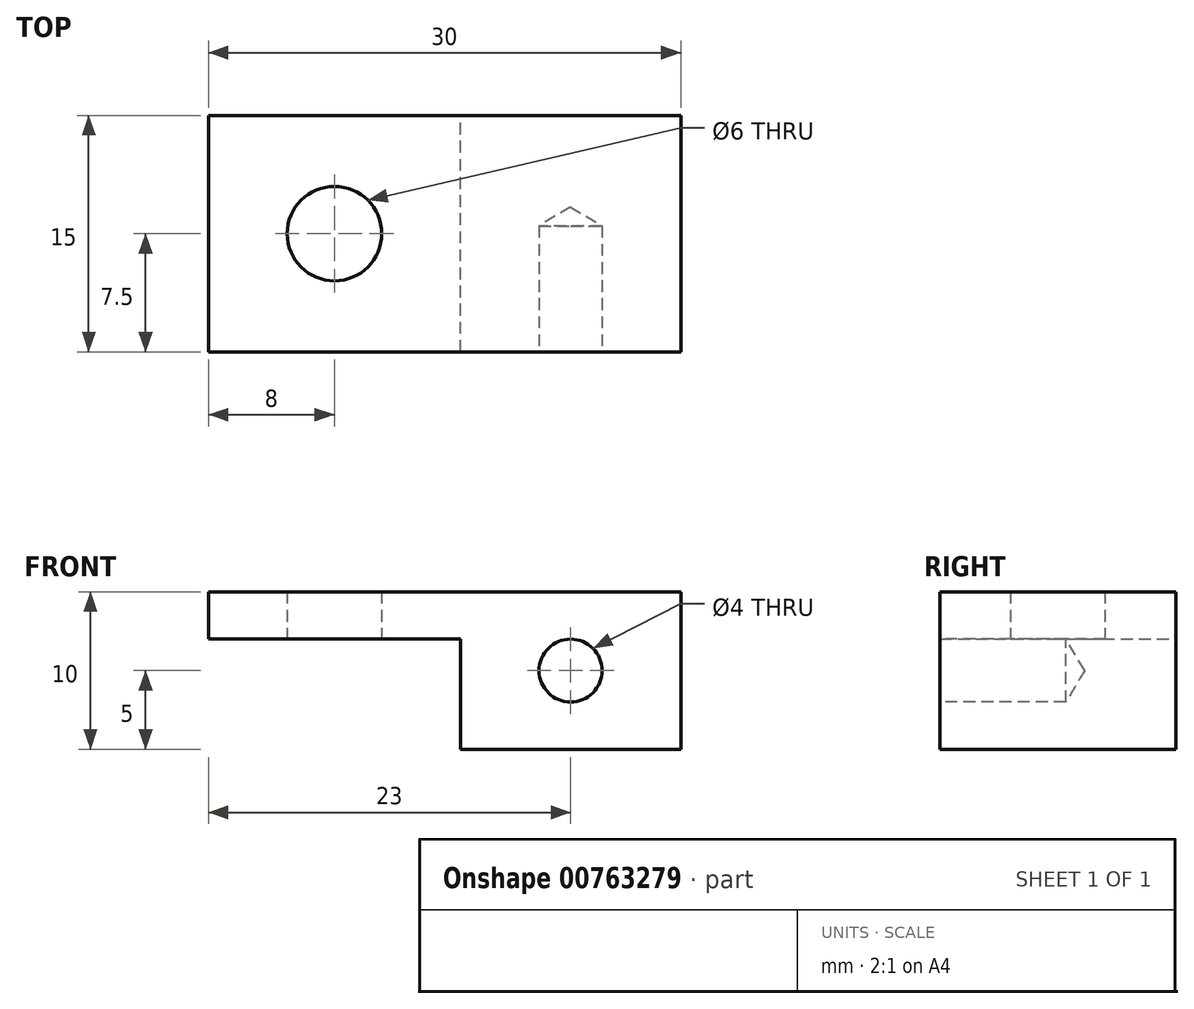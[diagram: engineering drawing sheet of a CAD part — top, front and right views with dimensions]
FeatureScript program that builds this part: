
annotation { "Feature Type Name" : "Feature", "Feature Type Description" : "" }
export const myFeature = defineFeature(function(context is Context, id is Id, definition is map)
    precondition{}
    {
        {
            var Q0;
            Q0=qCreatedBy(makeId("Top.planeOp"),FACE);
            var sketch = newSketch(context, id + "F0", { "sketchPlane" : qUnion([Q0])});
            skLineSegment(sketch, "E0.bottom", {"start": v(15, -7.5) * mm, "end": v(-15, -7.5) * mm});
            skLineSegment(sketch, "E0.top", {"start": v(15, 7.5) * mm, "end": v(-15, 7.5) * mm});
            skLineSegment(sketch, "E0.left", {"start": v(15, -7.5) * mm, "end": v(15, 7.5) * mm});
            skLineSegment(sketch, "E0.right", {"start": v(-15, -7.5) * mm, "end": v(-15, 7.5) * mm});
            skPoint(sketch, "E0.middle", {"position": v(0, 0) * mm});
            skPoint(sketch, "E1", {"position": v(-7, 0) * mm});
            skSolve(sketch);
        }
        {
            var Q0;
            Q0=qSketchRegion(id+"F0",true);
            extrude(context, id + "F1", {"entities" : qUnion([Q0]), "depth" : 10 * mm, "offsetDistance" : 25 * mm});
        }
        {
            var Q0;
            Q0=sQuery(id+"F0.wireOp",VERTEX,"E1");
            var Q1;
            Q1=makeQuery(id+"F1.opExtrude","SWEPT_BODY",BODY,{"disambiguationData":[OSD([sQuery(id+"F0.wireOp",EDGE,"E0.bottom"),sQuery(id+"F0.wireOp",EDGE,"E0.top"),sQuery(id+"F0.wireOp",EDGE,"E0.left"),sQuery(id+"F0.wireOp",EDGE,"E0.right")])]});
            hole(context, id + "F2", {"style" : HoleStyle.SIMPLE, "endStyle" : HoleEndStyle.THROUGH, "oppositeDirection" : true, "holeDiameter" : 6 * mm, "majorDiameter" : 5 * mm, "isTappedThrough" : true, "tappedDepth" : 12 * mm, "tapClearance" : 3, "locations" : qUnion([Q0]), "scope" : qUnion([Q1])});
        }
        {
            var Q0;
            Q0=makeQuery(id+"F1.opExtrude","SWEPT_FACE",FACE,{"disambiguationData":[OSD([sQuery(id+"F0.wireOp",EDGE,"E0.bottom")])]});
            var sketch = newSketch(context, id + "F3", { "sketchPlane" : qUnion([Q0])});
            skPoint(sketch, "E2", {"position": v(8, 5) * mm});
            skSolve(sketch);
        }
        {
            var Q0;
            Q0=sQuery(id+"F3.wireOp",VERTEX,"E2");
            var Q1;
            Q1=makeQuery(id+"F1.opExtrude","SWEPT_BODY",BODY,{"disambiguationData":[OSD([sQuery(id+"F0.wireOp",EDGE,"E0.bottom"),sQuery(id+"F0.wireOp",EDGE,"E0.top"),sQuery(id+"F0.wireOp",EDGE,"E0.left"),sQuery(id+"F0.wireOp",EDGE,"E0.right")])]});
            hole(context, id + "F4", {"style" : HoleStyle.SIMPLE, "endStyle" : HoleEndStyle.BLIND, "holeDiameter" : 4 * mm, "majorDiameter" : 5 * mm, "holeDepth" : 8 * mm, "isTappedThrough" : true, "tappedDepth" : 12 * mm, "tapClearance" : 3, "locations" : qUnion([Q0]), "scope" : qUnion([Q1])});
        }
        {
            var Q0;
            Q0=qCreatedBy(makeId("Front.planeOp"),FACE);
            var sketch = newSketch(context, id + "F5", { "sketchPlane" : qUnion([Q0])});
            skLineSegment(sketch, "E3.bottom", {"start": v(1, 0) * mm, "end": v(-15, 0) * mm});
            skLineSegment(sketch, "E3.top", {"start": v(1, 7) * mm, "end": v(-15, 7) * mm});
            skLineSegment(sketch, "E3.left", {"start": v(1, 0) * mm, "end": v(1, 7) * mm});
            skLineSegment(sketch, "E3.right", {"start": v(-15, 0) * mm, "end": v(-15, 7) * mm});
            skPoint(sketch, "E3.middle", {"position": v(-7, 3.5) * mm});
            skSolve(sketch);
        }
        {
            var Q0;
            Q0 = qSketchRegion(id + "F5", true);
            extrude(context, id + "F6", {"entities" : qUnion([Q0]), "operationType" : NewBodyOperationType.REMOVE, "endBound" : BoundingType.SYMMETRIC, "depth" : 15 * mm, "offsetDistance" : 25 * mm});
        }
    });
